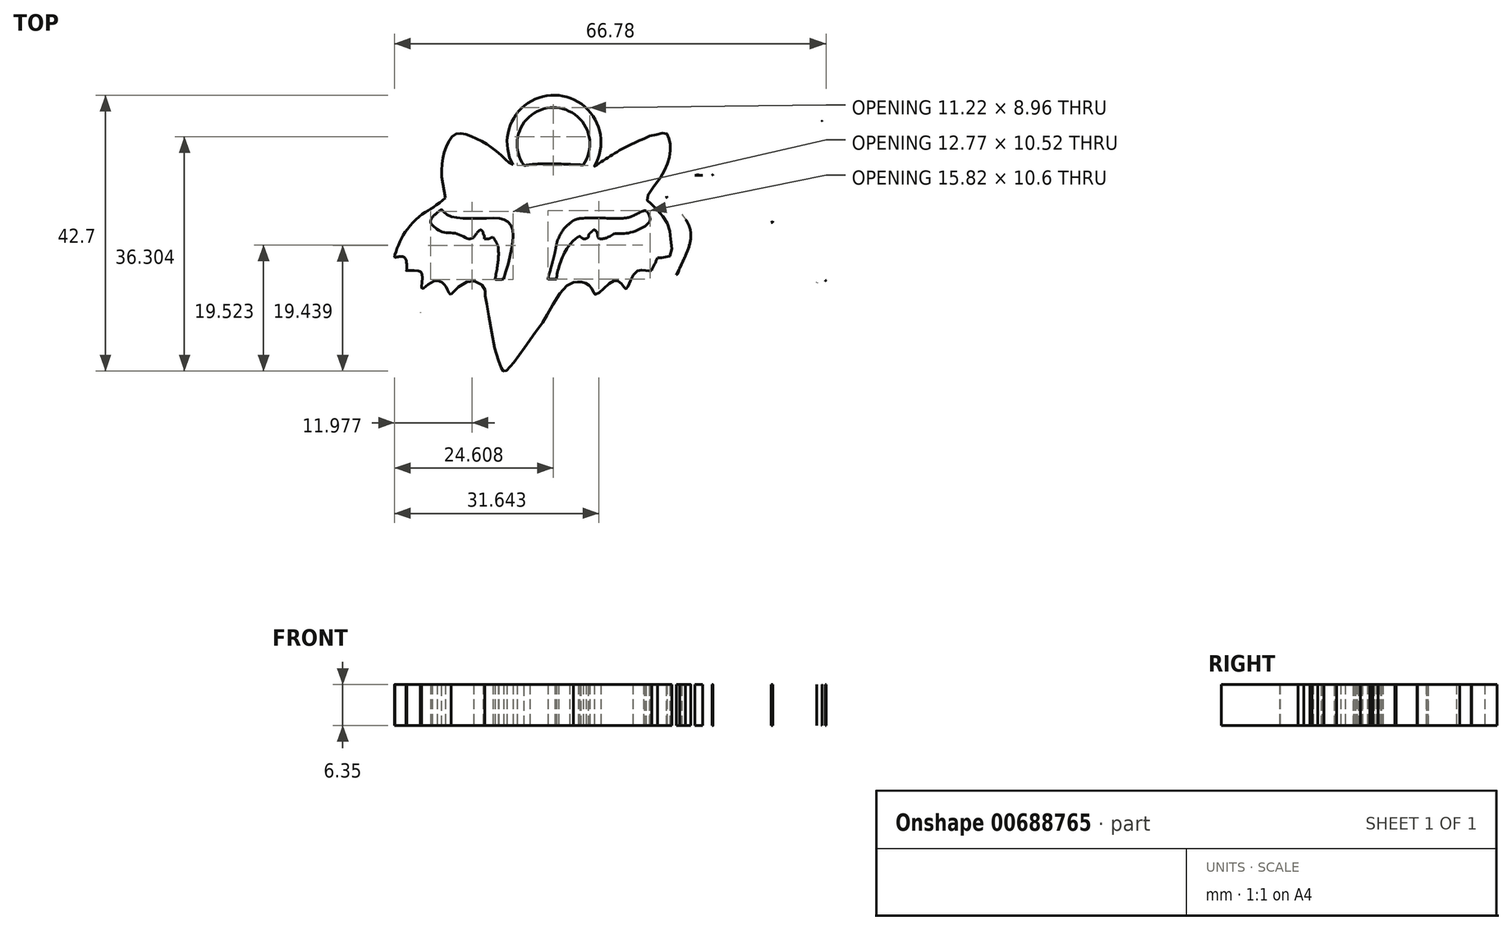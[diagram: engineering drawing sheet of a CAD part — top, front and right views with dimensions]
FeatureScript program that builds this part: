
annotation { "Feature Type Name" : "Feature", "Feature Type Description" : "" }
export const myFeature = defineFeature(function(context is Context, id is Id, definition is map)
    precondition{}
    {
        {
            var Q0;
            Q0=qCreatedBy(makeId("Top.planeOp"),FACE);
            var sketch = newSketch(context, id + "F0", { "sketchPlane" : qUnion([Q0])});
            skSolve(sketch);
        }
        {
            var Q0;
            Q0=qCreatedBy(makeId("Top.planeOp"),FACE);
            var sketch = newSketch(context, id + "F1", { "sketchPlane" : qUnion([Q0])});
            skLineSegment(sketch, "E0", {"start": v(-49.09, -7.95) * mm, "end": v(-49.09, -7.95) * mm});
            skLineSegment(sketch, "E1", {"start": v(-25.67, 10.6) * mm, "end": v(-25.67, 10.9) * mm});
            skFitSpline(sketch, "E2", {"points": [v(-47.91, 14.68) * mm, v(-18.42, 14.68) * mm], "startDerivative": vector(29.5, 0) * mm, "endDerivative": vector(29.5, 0) * mm});
            skFitSpline(sketch, "E3", {"points": [v(-18.42, 14.77) * mm, v(-19.98, 12.11) * mm, v(-20.27, 10.35) * mm, v(-20.02, 7.92) * mm], "startDerivative": vector(-4.98, -7.4) * mm, "endDerivative": vector(1.02, -7.61) * mm});
            skFitSpline(sketch, "E4", {"points": [v(-4, -7.29) * mm, v(-5.22, -7.31) * mm, v(-5.3, -7.27) * mm], "startDerivative": vector(-2, -0.12) * mm, "endDerivative": vector(-0.28, 0.23) * mm});
            skFitSpline(sketch, "E5", {"points": [v(-5.3, -7.27) * mm, v(-4.8, -4.13) * mm, v(-4.8, -2.31) * mm], "startDerivative": vector(1.15, 5.88) * mm, "endDerivative": vector(-0.2, 3.94) * mm});
            skFitSpline(sketch, "E6", {"points": [v(-4.8, -2.31) * mm, v(-5.1, -1.62) * mm, v(-5.66, -0.73) * mm], "startDerivative": vector(-0.57, 1.49) * mm, "endDerivative": vector(-1.14, 1.67) * mm});
            skFitSpline(sketch, "E7", {"points": [v(-5.66, -0.73) * mm, v(-6.33, -1.03) * mm, v(-6.94, -1.03) * mm], "startDerivative": vector(-1.29, -0.72) * mm, "endDerivative": vector(-1.27, 0.14) * mm});
            skFitSpline(sketch, "E8", {"points": [v(-6.94, -1.1) * mm, v(-6.94, -1.03) * mm], "startDerivative": vector(0, 0.07) * mm, "endDerivative": vector(0, 0.07) * mm});
            skFitSpline(sketch, "E9", {"points": [v(-6.94, -1.1) * mm, v(-6.94, -0.48) * mm], "startDerivative": vector(0, 0.63) * mm, "endDerivative": vector(0, 0.63) * mm});
            skFitSpline(sketch, "E10", {"points": [v(-6.94, -0.48) * mm, v(-7.16, -0.32) * mm, v(-7.13, 0) * mm], "startDerivative": vector(-0.6, 0.26) * mm, "endDerivative": vector(0.21, 0.7) * mm});
            skFitSpline(sketch, "E11", {"points": [v(-7.13, 0) * mm, v(-7.56, 0.34) * mm, v(-8.61, -0.86) * mm], "startDerivative": vector(-1.1, 1.43) * mm, "endDerivative": vector(-1.82, -2.79) * mm});
            skFitSpline(sketch, "E12", {"points": [v(-8.61, -0.86) * mm, v(-9.38, -1.03) * mm, v(-11.22, -0.25) * mm, v(-13.42, 0) * mm, v(-15.04, 1.1) * mm], "startDerivative": vector(-4.09, -2) * mm, "endDerivative": vector(-5.54, 5.18) * mm});
            skFitSpline(sketch, "E13", {"points": [v(-15.04, 1.1) * mm, v(-15.29, 1.57) * mm, v(-15.04, 2.26) * mm, v(-14.25, 3) * mm], "startDerivative": vector(-1.25, 1.57) * mm, "endDerivative": vector(2.2, 1.8) * mm});
            skFitSpline(sketch, "E14", {"points": [v(-14.25, 3) * mm, v(-13.92, 3.28) * mm, v(-13.62, 3.51) * mm, v(-13.15, 3) * mm, v(-12.16, 2.43) * mm, v(-10.27, 2.14) * mm, v(-6.94, 2.14) * mm, v(-4.43, 2.12) * mm, v(-3.47, 1.7) * mm, v(-2.7, 0.75) * mm, v(-2.52, -0.98) * mm, v(-3.06, -4.07) * mm, v(-4, -7.29) * mm], "startDerivative": vector(7.65, 5.48) * mm, "endDerivative": vector(-8.33, -25.98) * mm});
            skFitSpline(sketch, "E15", {"points": [v(7.89, -0.68) * mm, v(8.34, -1.01) * mm, v(8.8, -0.99) * mm, v(9.19, -0.68) * mm, v(9.19, -0.43) * mm, v(9.58, 0) * mm, v(10, 0.34) * mm, v(10.47, 0) * mm, v(10.59, -0.68) * mm, v(10.86, -1.01) * mm, v(11.58, -0.99) * mm, v(12.38, -0.68) * mm, v(13.22, -0.26) * mm, v(14.48, -0.21) * mm, v(16.58, 0.24) * mm, v(18.6, 1.67) * mm, v(18.54, 2.58) * mm, v(18.15, 3.22) * mm, v(17.69, 3.29) * mm, v(16.04, 2.52) * mm, v(14.14, 2.13) * mm, v(7.8, 2.12) * mm, v(7.8, 2.1) * mm], "startDerivative": vector(12.59, -11.48) * mm, "endDerivative": vector(1.85, -2.93) * mm});
            skFitSpline(sketch, "E16", {"points": [v(7.83, 2.1) * mm, v(7.8, 2.12) * mm, v(6.21, 1.32) * mm, v(4.53, -0.9) * mm, v(3.98, -3.04) * mm, v(3.6, -4.55) * mm, v(2.86, -7.29) * mm], "startDerivative": vector(-0.8, 0.97) * mm, "endDerivative": vector(-3.68, -13.47) * mm});
            skPoint(sketch, "E17.3.internal.snap0", {"position": v(-53.93, -7) * mm});
            skFitSpline(sketch, "E18", {"points": [v(-21.7, -6.22) * mm, v(-21.7, -8.4) * mm, v(-21.32, -9.37) * mm, v(-20.7, -10) * mm, v(-20.03, -9.32) * mm, v(-19.25, -8.66) * mm, v(-19.1, -9.52) * mm, v(-18.72, -10.73) * mm, v(-18.23, -11.67) * mm, v(-16.87, -12.4) * mm, v(-16.87, -12.46) * mm], "startDerivative": vector(-0.94, -16.44) * mm, "endDerivative": vector(-1.12, -2.05) * mm});
            skFitSpline(sketch, "E19", {"points": [v(-16.87, -12.46) * mm, v(-16.38, -11.54) * mm, v(-15.6, -10.64) * mm, v(-15.05, -10.16) * mm, v(-14.65, -11.22) * mm, v(-14.1, -12.1) * mm, v(-13.36, -12.83) * mm, v(-12.23, -13.45) * mm, v(-12.23, -13.47) * mm], "startDerivative": vector(3.11, 6.8) * mm, "endDerivative": vector(-0.47, -0.82) * mm});
            skFitSpline(sketch, "E20", {"points": [v(-12.23, -13.46) * mm, v(-11.6, -12.44) * mm], "startDerivative": vector(0.62, 1.02) * mm, "endDerivative": vector(0.62, 1.02) * mm});
            skFitSpline(sketch, "E21", {"points": [v(15.9, -10.84) * mm, v(16.57, -10.17) * mm, v(17.08, -9.37) * mm, v(17.42, -8.8) * mm, v(17.78, -8.73) * mm, v(18.08, -9.22) * mm, v(18.2, -9.76) * mm, v(18.44, -9.97) * mm, v(18.82, -9.76) * mm, v(19.28, -9.42) * mm, v(19.85, -8.78) * mm, v(20.32, -8.1) * mm, v(20.66, -7.35) * mm, v(20.67, -7.35) * mm], "startDerivative": vector(6.88, 6.38) * mm, "endDerivative": vector(0.9, -0.5) * mm});
            skFitSpline(sketch, "E22", {"points": [v(14.66, 15.21) * mm, v(17.54, 16.2) * mm, v(21.2, 17) * mm, v(22.88, 17.22) * mm, v(24.07, 14.55) * mm, v(24.17, 11.37) * mm, v(24.18, 11.37) * mm], "startDerivative": vector(13.27, 5.32) * mm, "endDerivative": vector(1.02, 0.5) * mm});
            skFitSpline(sketch, "E23", {"points": [v(24.18, 11.38) * mm, v(21.23, 5.36) * mm, v(21.23, 5.53) * mm], "startDerivative": vector(-4.9, -10.54) * mm, "endDerivative": vector(0.24, 1.82) * mm});
            skFitSpline(sketch, "E24", {"points": [v(21.23, 5.53) * mm, v(23.53, 2.89) * mm, v(24.97, 0) * mm, v(24.18, -3.63) * mm, v(22.73, -6.6) * mm], "startDerivative": vector(9.4, -10.26) * mm, "endDerivative": vector(-6.1, -11.5) * mm});
            skFitSpline(sketch, "E25", {"points": [v(34.28, 1.1) * mm, v(33.07, 2.83) * mm, v(28.3, 8.87) * mm, v(28.42, 8.8) * mm], "startDerivative": vector(-2.16, 3.59) * mm, "endDerivative": vector(2.19, -1.55) * mm});
            skFitSpline(sketch, "E26", {"points": [v(28.42, 8.8) * mm, v(24.18, 8.8) * mm], "startDerivative": vector(-4.24, 0) * mm, "endDerivative": vector(-4.24, 0) * mm});
            skFitSpline(sketch, "E27", {"points": [v(45.28, 17.22) * mm, v(45.28, 17.2) * mm, v(24.18, 17.2) * mm], "startDerivative": vector(0.33, -0.69) * mm, "endDerivative": vector(-32.31, 0.33) * mm});
            skFitSpline(sketch, "E28", {"points": [v(45.29, 17.22) * mm, v(43.56, 9.5) * mm], "startDerivative": vector(-1.72, -7.72) * mm, "endDerivative": vector(-1.72, -7.72) * mm});
            skFitSpline(sketch, "E29", {"points": [v(43.56, 9.5) * mm, v(44.34, 8.34) * mm], "startDerivative": vector(0.78, -1.16) * mm, "endDerivative": vector(0.78, -1.16) * mm});
            skFitSpline(sketch, "E30", {"points": [v(44.34, 8.34) * mm, v(45.69, 9.5) * mm], "startDerivative": vector(1.34, 1.16) * mm, "endDerivative": vector(1.34, 1.16) * mm});
            skFitSpline(sketch, "E31", {"points": [v(47.66, 17.2) * mm, v(68.11, 17.2) * mm], "startDerivative": vector(20.45, 0) * mm, "endDerivative": vector(20.45, 0) * mm});
            skFitSpline(sketch, "E32", {"points": [v(68.11, 17.33) * mm, v(66.26, 8.93) * mm], "startDerivative": vector(-1.85, -8.4) * mm, "endDerivative": vector(-1.85, -8.4) * mm});
            skFitSpline(sketch, "E33", {"points": [v(60.99, 8.93) * mm, v(51.26, 1.06) * mm, v(51.24, 1.02) * mm], "startDerivative": vector(-14.98, -11.94) * mm, "endDerivative": vector(-0.07, -0.46) * mm});
            skFitSpline(sketch, "E34", {"points": [v(16.52, -14.6) * mm, v(16.95, -14.62) * mm], "startDerivative": vector(0.43, -0.01) * mm, "endDerivative": vector(0.43, -0.01) * mm});
            skFitSpline(sketch, "E35", {"points": [v(27.54, 7.05) * mm, v(31.94, 1.5) * mm, v(31.91, 1.48) * mm], "startDerivative": vector(7.07, -8.52) * mm, "endDerivative": vector(-0.53, -0.19) * mm});
            skFitSpline(sketch, "E36", {"points": [v(26.23, -2.36) * mm, v(26.4, -0.97) * mm, v(26.23, 0.64) * mm, v(25.75, 2.5) * mm, v(23.15, 5.64) * mm, v(23.12, 5.59) * mm], "startDerivative": vector(1.34, 6.98) * mm, "endDerivative": vector(-0.1, -1.92) * mm});
            skFitSpline(sketch, "E37", {"points": [v(46.35, -6.63) * mm, v(45.9, -7.47) * mm, v(45.28, -7.81) * mm, v(44.5, -7.81) * mm, v(44.5, -7.78) * mm], "startDerivative": vector(-1.16, -2.79) * mm, "endDerivative": vector(0.23, 0.5) * mm});
            skFitSpline(sketch, "E38", {"points": [v(44.5, -7.78) * mm, v(43.44, -12.63) * mm], "startDerivative": vector(-1.06, -4.85) * mm, "endDerivative": vector(-1.06, -4.85) * mm});
            skFitSpline(sketch, "E39", {"points": [v(-12.98, 5.32) * mm, v(-13.54, 8.65) * mm, v(-13.4, 11.41) * mm, v(-12.71, 13.57) * mm, v(-11.39, 15.2) * mm, v(-9.69, 15.08) * mm, v(-7.6, 14.17) * mm, v(-5.72, 13) * mm, v(-3.75, 11.34) * mm, v(-2.54, 10.43) * mm, v(-0.8, 10.32) * mm, v(2, 10.58) * mm, v(10.05, 10.2) * mm, v(10.08, 10.16) * mm], "startDerivative": vector(-7.87, 36.08) * mm, "endDerivative": vector(0.56, -3.15) * mm});
            skFitSpline(sketch, "E40", {"points": [v(10.08, 10.16) * mm, v(14.05, 12.7) * mm, v(18.65, 14.87) * mm], "startDerivative": vector(7.87, 5.39) * mm, "endDerivative": vector(9.26, 4.03) * mm});
            skFitSpline(sketch, "E41", {"points": [v(18.65, 14.87) * mm, v(20.13, 15.21) * mm, v(21.16, 15.32) * mm, v(21.6, 14.5) * mm, v(21.82, 13.37) * mm, v(21.72, 11.89) * mm, v(21.23, 10.16) * mm, v(20.07, 8.1) * mm, v(18.15, 5.25) * mm, v(18.54, 4.64) * mm, v(20.15, 3.09) * mm, v(21.54, 0.94) * mm, v(21.94, -1.56) * mm, v(21.59, -3.84) * mm, v(19.82, -3.93) * mm, v(19.83, -3.96) * mm], "startDerivative": vector(22.87, 4.8) * mm, "endDerivative": vector(3.6, -3.57) * mm});
            skFitSpline(sketch, "E42", {"points": [v(19.83, -3.96) * mm, v(18.92, -5.95) * mm, v(18.9, -6) * mm], "startDerivative": vector(-1.44, -3.14) * mm, "endDerivative": vector(-0.11, -0.21) * mm});
            skFitSpline(sketch, "E43", {"points": [v(18.92, -5.95) * mm, v(18.15, -5.95) * mm, v(16.45, -6.2) * mm, v(14.98, -8.75) * mm, v(14.38, -8.1) * mm, v(13.02, -7.55) * mm, v(10.31, -9.64) * mm, v(9.69, -8.8) * mm, v(8.4, -7.77) * mm, v(6.84, -7.75) * mm], "startDerivative": vector(-8.8, -0.7) * mm, "endDerivative": vector(-14.52, -1.73) * mm});
            skFitSpline(sketch, "E44", {"points": [v(6.84, -7.75) * mm, v(5.17, -8.86) * mm, v(2.87, -12.64) * mm, v(1.24, -15.11) * mm, v(-3.39, -21.31) * mm, v(-3.82, -21.5) * mm, v(-4.08, -21.47) * mm, v(-4.32, -21.03) * mm, v(-5.22, -18.5) * mm, v(-6.47, -11.76) * mm, v(-6.87, -9.64) * mm, v(-6.87, -8.82) * mm, v(-7.98, -7.75) * mm, v(-9.88, -7.77) * mm, v(-12.09, -9.64) * mm], "startDerivative": vector(-24.53, -10.71) * mm, "endDerivative": vector(-26.27, -28.08) * mm});
            skFitSpline(sketch, "E45", {"points": [v(-12.09, -9.64) * mm, v(-12.43, -9.44) * mm, v(-12.92, -8.4) * mm, v(-13.98, -7.55) * mm, v(-15.15, -7.77) * mm, v(-16.3, -8.6) * mm, v(-16.61, -8.68) * mm, v(-16.6, -6.6) * mm, v(-17.29, -5.95) * mm, v(-19.07, -5.95) * mm, v(-18.98, -5.95) * mm], "startDerivative": vector(-5.61, 1.85) * mm, "endDerivative": vector(4.73, 0.11) * mm});
            skFitSpline(sketch, "E46", {"points": [v(-12.98, 5.32) * mm, v(-14.82, 3.87) * mm, v(-16.38, 2.9) * mm, v(-18.37, 1.07) * mm, v(-19.77, -0.92) * mm, v(-20.59, -2.87) * mm, v(-20.86, -3.89) * mm, v(-20.82, -3.92) * mm], "startDerivative": vector(-10.8, -9.13) * mm, "endDerivative": vector(1.8, -0.8) * mm});
            skFitSpline(sketch, "E47", {"points": [v(-20.82, -3.92) * mm, v(-19.31, -3.92) * mm, v(-18.98, -5.95) * mm], "startDerivative": vector(3.88, 0.87) * mm, "endDerivative": vector(-0.09, -4.78) * mm});
            skFitSpline(sketch, "E48", {"points": [v(-14.8, 18.65) * mm, v(-51.24, 18.6) * mm], "startDerivative": vector(-36.44, -0.05) * mm, "endDerivative": vector(-36.44, -0.05) * mm});
            skFitSpline(sketch, "E49", {"points": [v(45.9, 19.18) * mm, v(46.51, 18.7) * mm, v(47.11, 19.18) * mm, v(47.05, 19.18) * mm], "startDerivative": vector(1.17, -1.83) * mm, "endDerivative": vector(-0.72, -0.2) * mm});
            skFitSpline(sketch, "E50", {"points": [v(47.05, 19.12) * mm, v(68.94, 19.18) * mm, v(69, 19.18) * mm], "startDerivative": vector(33.36, 0.1) * mm, "endDerivative": vector(0.6, 0) * mm});
            skFitSpline(sketch, "E51", {"points": [v(70.13, 17.33) * mm, v(67.86, 8.3) * mm, v(67.5, 7.53) * mm, v(66.88, 7.08) * mm, v(61.43, 7.12) * mm, v(62.89, 6.68) * mm, v(64.3, 6.03) * mm, v(65.52, 5.1) * mm, v(66.49, 3.8) * mm, v(66.88, 2.35) * mm, v(67.08, 0.44) * mm, v(66.48, -1.36) * mm, v(65.5, -2.71) * mm, v(64.05, -3.84) * mm, v(62.77, -4.5) * mm, v(61.87, -4.8) * mm, v(62.77, -4.87) * mm, v(63.78, -5.4) * mm, v(64.4, -6.4) * mm, v(64.28, -7.62) * mm, v(63.85, -9.43) * mm, v(62.41, -15.26) * mm, v(62.1, -15.78) * mm, v(61.84, -16.1) * mm, v(61.55, -16.3) * mm, v(61.23, -16.49) * mm, v(61.34, -16.5) * mm], "startDerivative": vector(-27.67, -120.8) * mm, "endDerivative": vector(15.83, 0.17) * mm});
            skFitSpline(sketch, "E52", {"points": [v(38.2, -16.5) * mm, v(16.28, -16.5) * mm, v(16.27, -16.5) * mm], "startDerivative": vector(-33.14, 0) * mm, "endDerivative": vector(-0.27, 0) * mm});
            skFitSpline(sketch, "E53", {"points": [v(-49.09, -7.95) * mm, v(-49.46, -8.44) * mm], "startDerivative": vector(-0.37, -0.5) * mm, "endDerivative": vector(-0.37, -0.5) * mm});
            skFitSpline(sketch, "E54", {"points": [v(-39.43, -9) * mm, v(-38.96, -9.14) * mm], "startDerivative": vector(0.47, -0.13) * mm, "endDerivative": vector(0.47, -0.13) * mm});
            skPoint(sketch, "E55.start.orphan", {"position": v(5.02, -4.59) * mm});
            skPoint(sketch, "E56.0.internal.orphan", {"position": v(7.6, -0.68) * mm});
            skPoint(sketch, "E56.endDerivative.orphan", {"position": v(7.8, -0.68) * mm});
            skFitSpline(sketch, "E57", {"points": [v(2.86, -7.29) * mm, v(4.2, -7.29) * mm], "startDerivative": vector(1.34, 0) * mm, "endDerivative": vector(1.34, 0) * mm});
            skFitSpline(sketch, "E58", {"points": [v(4.2, -7.29) * mm, v(4.28, -6.64) * mm, v(4.47, -5.79) * mm, v(4.82, -4.69) * mm, v(5.34, -3.4) * mm, v(6.13, -2.1) * mm, v(7.6, -0.68) * mm, v(7.8, -0.68) * mm, v(7.89, -0.68) * mm, v(8.04, -0.82) * mm, v(8.34, -1.01) * mm, v(8.8, -0.99) * mm, v(9.19, -0.68) * mm, v(9.19, -0.43) * mm, v(9.58, 0) * mm, v(10, 0.34) * mm, v(10.47, 0) * mm, v(10.59, -0.68) * mm, v(10.86, -1.01) * mm, v(11.58, -0.99) * mm, v(12.38, -0.68) * mm, v(13.22, -0.26) * mm, v(14.48, -0.21) * mm, v(16.58, 0.24) * mm, v(18.6, 1.67) * mm, v(18.54, 2.58) * mm, v(18.15, 3.22) * mm, v(17.69, 3.29) * mm, v(16.04, 2.52) * mm, v(14.14, 2.13) * mm, v(7.83, 2.1) * mm, v(6.21, 1.32) * mm, v(4.53, -0.9) * mm, v(3.98, -3.04) * mm, v(3.6, -4.55) * mm, v(3.13, -6.3) * mm, v(2.86, -7.29) * mm], "startDerivative": vector(2.77, 28.84) * mm, "endDerivative": vector(-9.04, -33) * mm});
            skPoint(sketch, "E59.1.internal.orphan", {"position": v(27.9, 15.3) * mm});
            skPoint(sketch, "E60.1.internal.orphan", {"position": v(29.24, 10.91) * mm});
            skPoint(sketch, "E61.1.internal.orphan", {"position": v(27.9, 11.11) * mm});
            skPoint(sketch, "E62.1.internal.orphan", {"position": v(41.93, 15.3) * mm});
            skPoint(sketch, "E62.2.internal.orphan", {"position": v(41.94, 15.35) * mm});
            skPoint(sketch, "E63.10.internal.orphan", {"position": v(41.25, 7.05) * mm});
            skPoint(sketch, "E63.11.internal.orphan", {"position": v(40.22, 8.27) * mm});
            skPoint(sketch, "E63.12.internal.orphan", {"position": v(39.44, 9.11) * mm});
            skPoint(sketch, "E63.13.internal.orphan", {"position": v(39.17, 9.5) * mm});
            skPoint(sketch, "E63.15.internal.orphan", {"position": v(40.84, 11.16) * mm});
            skPoint(sketch, "E63.16.internal.orphan", {"position": v(41.1, 11.16) * mm});
            skPoint(sketch, "E63.4.internal.orphan", {"position": v(49.54, 9.5) * mm});
            skPoint(sketch, "E63.5.internal.orphan", {"position": v(46.73, 7.05) * mm});
            skPoint(sketch, "E63.7.internal.orphan", {"position": v(44.14, 5.64) * mm});
            skPoint(sketch, "E63.8.internal.orphan", {"position": v(43.44, 5.64) * mm});
            skPoint(sketch, "E63.startDerivative.orphan", {"position": v(49.28, 11.11) * mm});
            skPoint(sketch, "E64.1.internal.orphan", {"position": v(35.4, -12.63) * mm});
            skPoint(sketch, "E65.1.internal.orphan", {"position": v(20.32, -11.56) * mm});
            skPoint(sketch, "E65.start.orphan", {"position": v(20.18, -12.63) * mm});
            skPoint(sketch, "E66.5.internal.orphan", {"position": v(35.4, -7.24) * mm});
            skPoint(sketch, "E66.6.internal.orphan", {"position": v(35.4, -6.88) * mm});
            skPoint(sketch, "E67.1.internal.orphan", {"position": v(39.17, -3.72) * mm});
            skPoint(sketch, "E67.2.internal.orphan", {"position": v(40.8, -3.04) * mm});
            skPoint(sketch, "E67.3.internal.orphan", {"position": v(43.38, -3.04) * mm});
            skPoint(sketch, "E67.5.internal.orphan", {"position": v(46.03, -5.7) * mm});
            skPoint(sketch, "E68.1.internal.orphan", {"position": v(58.77, -12.63) * mm});
            skPoint(sketch, "E68.2.internal.orphan", {"position": v(58.86, -12.63) * mm});
            skPoint(sketch, "E69.1.internal.orphan", {"position": v(52.7, -3.92) * mm});
            skPoint(sketch, "E70.0.internal.orphan", {"position": v(59.63, -8.44) * mm});
            skPoint(sketch, "E70.1.internal.orphan", {"position": v(57.17, -8.44) * mm});
            skPoint(sketch, "E70.2.internal.orphan", {"position": v(57.13, -8.44) * mm});
            skPoint(sketch, "E71.1.internal.orphan", {"position": v(50, 15.3) * mm});
            skPoint(sketch, "E72.end.orphan", {"position": v(49.1, 11.16) * mm});
            skPoint(sketch, "E72.start.orphan", {"position": v(50, 15.35) * mm});
            skPoint(sketch, "E73.1.internal.orphan", {"position": v(63.84, 10.91) * mm});
            skPoint(sketch, "E73.2.internal.orphan", {"position": v(63.88, 10.91) * mm});
            skPoint(sketch, "E74.end.orphan", {"position": v(64.87, 15.3) * mm});
            skPoint(sketch, "E75.startDerivative.orphan", {"position": v(46.35, 12.07) * mm});
            skPoint(sketch, "E76.startDerivative.orphan", {"position": v(47.15, -14.56) * mm});
            skPoint(sketch, "E77.0.internal.orphan", {"position": v(40.22, -14.53) * mm});
            skPoint(sketch, "E77.1.internal.orphan", {"position": v(42.06, -6.4) * mm});
            skPoint(sketch, "E77.startDerivative.orphan", {"position": v(40.84, -11.82) * mm});
            skPoint(sketch, "E78.1.internal.orphan", {"position": v(37.92, -14.56) * mm});
            skPoint(sketch, "E78.startDerivative.orphan", {"position": v(39.17, -9.12) * mm});
            skPoint(sketch, "E79.1.internal.orphan", {"position": v(39.8, -6.4) * mm});
            skPoint(sketch, "E79.startDerivative.orphan", {"position": v(40.8, -5.7) * mm});
            skPoint(sketch, "E80.1.internal.orphan", {"position": v(48.07, 1.06) * mm});
            skPoint(sketch, "E81.end.orphan", {"position": v(60.15, 10.91) * mm});
            skPoint(sketch, "E82.1.internal.orphan", {"position": v(24.18, 9.95) * mm});
            skPoint(sketch, "E82.2.internal.orphan", {"position": v(25.08, 11.37) * mm});
            skPoint(sketch, "E83.endDerivative.orphan", {"position": v(31.22, -0.97) * mm});
            skPoint(sketch, "E83.startDerivative.orphan", {"position": v(28.15, -3.04) * mm});
            skPoint(sketch, "E84.end.orphan", {"position": v(25.08, -5.1) * mm});
            skPoint(sketch, "E85.endDerivative.orphan", {"position": v(56.06, -3.92) * mm});
            skPoint(sketch, "E86.0.internal.orphan", {"position": v(58.46, -6.4) * mm});
            skPoint(sketch, "E86.1.internal.orphan", {"position": v(62.77, -6.4) * mm});
            skPoint(sketch, "E87.1.internal.orphan", {"position": v(60.99, -14.76) * mm});
            skPoint(sketch, "E87.2.internal.orphan", {"position": v(60.99, -14.62) * mm});
            skFitSpline(sketch, "E88", {"points": [v(24.18, 17.2) * mm, v(25.08, 11.37) * mm, v(24.18, 9.95) * mm, v(24.18, 8.8) * mm, v(25.6, 8.8) * mm, v(27, 8.8) * mm, v(28.36, 8.85) * mm, v(28.42, 8.8) * mm], "startDerivative": vector(6.68, -24.74) * mm, "endDerivative": vector(1, -1.51) * mm});
            skFitSpline(sketch, "E89", {"points": [v(37.68, 1.65) * mm, v(20.32, -11.56) * mm, v(20.18, -12.63) * mm], "startDerivative": vector(-29.6, -20.36) * mm, "endDerivative": vector(1.1, -4.94) * mm});
            skFitSpline(sketch, "E90", {"points": [v(36.42, -7.87) * mm, v(35.4, -7.24) * mm, v(35.4, -6.88) * mm, v(39.17, -3.72) * mm, v(40.8, -3.04) * mm, v(43.38, -3.04) * mm, v(46.03, -5.7) * mm, v(46.35, -6.63) * mm, v(45.9, -7.47) * mm, v(45.28, -7.81) * mm, v(44.5, -7.78) * mm, v(44.15, -9.4) * mm, v(43.8, -11.01) * mm, v(43.44, -12.63) * mm], "startDerivative": vector(-18.94, 9.98) * mm, "endDerivative": vector(-4.26, -21.04) * mm});
            skFitSpline(sketch, "E91", {"points": [v(58.86, -12.63) * mm, v(43.44, -12.63) * mm], "startDerivative": vector(-15.42, 0) * mm, "endDerivative": vector(-15.42, 0) * mm});
            skFitSpline(sketch, "E92", {"points": [v(41.94, 15.35) * mm, v(41.1, 11.16) * mm], "startDerivative": vector(-0.85, -4.19) * mm, "endDerivative": vector(-0.85, -4.19) * mm});
            skFitSpline(sketch, "E93", {"points": [v(41.1, 11.16) * mm, v(40.84, 11.16) * mm, v(39.17, 9.5) * mm, v(39.44, 9.11) * mm, v(40.22, 8.27) * mm, v(41.25, 7.05) * mm, v(43.44, 5.64) * mm, v(44.14, 5.64) * mm, v(46.73, 7.05) * mm, v(49.54, 9.5) * mm, v(49.28, 11.11) * mm], "startDerivative": vector(-4.41, 2.3) * mm, "endDerivative": vector(-6.82, 15.52) * mm});
            skFitSpline(sketch, "E94", {"points": [v(49.28, 11.11) * mm, v(49.1, 11.16) * mm, v(50, 15.35) * mm], "startDerivative": vector(-1.24, -0.16) * mm, "endDerivative": vector(2, 7.06) * mm});
            skFitSpline(sketch, "E95", {"points": [v(40.84, 11.16) * mm, v(40.04, 10.87) * mm, v(39.53, 10.48) * mm, v(39.2, 10.1) * mm, v(39.17, 9.5) * mm], "startDerivative": vector(-2.98, -0.82) * mm, "endDerivative": vector(0.2, -2.7) * mm});
            skFitSpline(sketch, "E96", {"points": [v(63.88, 10.91) * mm, v(63.84, 10.91) * mm, v(60.15, 10.91) * mm], "startDerivative": vector(-0.24, 0) * mm, "endDerivative": vector(-5.73, 0) * mm});
            skPoint(sketch, "E97.1.internal.orphan", {"position": v(-35.18, -5.1) * mm});
            skPoint(sketch, "E97.2.internal.orphan", {"position": v(-34.84, -5.1) * mm});
            skPoint(sketch, "E97.3.internal.orphan", {"position": v(-33.24, -5.1) * mm});
            skPoint(sketch, "E97.4.internal.orphan", {"position": v(-31.14, -5.1) * mm});
            skPoint(sketch, "E97.5.internal.orphan", {"position": v(-26.01, -5.1) * mm});
            skPoint(sketch, "E98.right.end.orphan", {"position": v(-32.85, 6.76) * mm});
            skPoint(sketch, "E99.1.internal.orphan", {"position": v(-24.99, 9.6) * mm});
            skPoint(sketch, "E100.1.internal.orphan", {"position": v(-36.35, 9.6) * mm});
            skPoint(sketch, "E101.12.internal.orphan", {"position": v(-35.18, -5.29) * mm});
            skPoint(sketch, "E101.3.internal.orphan", {"position": v(-32.85, -15.53) * mm});
            skPoint(sketch, "E102.3.internal.orphan", {"position": v(-40.22, -5.43) * mm});
            skPoint(sketch, "E103.start.orphan", {"position": v(-37.36, -7) * mm});
            skPoint(sketch, "E104.14.internal.orphan", {"position": v(-52.8, -5.43) * mm});
            skPoint(sketch, "E104.17.internal.orphan", {"position": v(-57.63, -6.4) * mm});
            skPoint(sketch, "E105.start.orphan", {"position": v(-52.58, 8.2) * mm});
            skPoint(sketch, "E106.0.internal.orphan", {"position": v(-45.15, 8.2) * mm});
            skPoint(sketch, "E106.1.internal.orphan", {"position": v(-45.15, 9.36) * mm});
            skPoint(sketch, "E106.end.orphan", {"position": v(-48.96, 10.35) * mm});
            skPoint(sketch, "E107.orphan", {"position": v(-51.8, -7) * mm});
            skPoint(sketch, "E108.end.orphan", {"position": v(-56.07, -7) * mm});
            skPoint(sketch, "E109.end.orphan", {"position": v(-36.21, -9.14) * mm});
            skPoint(sketch, "E109.start.orphan", {"position": v(-37.11, -12.83) * mm});
            skPoint(sketch, "E110.21.internal.orphan", {"position": v(54.1, 0) * mm});
            skFitSpline(sketch, "E111.trimOffspring", {"points": [v(27.9, 11.11) * mm, v(29.24, 10.91) * mm, v(37.45, 1.49) * mm, v(37.68, 1.65) * mm], "startDerivative": vector(4.49, 2.04) * mm, "endDerivative": vector(1.27, 3.27) * mm});
            skPoint(sketch, "E112.1.internal.orphan", {"position": v(39.63, -16.5) * mm});
            skPoint(sketch, "E113.1.internal.orphan", {"position": v(38.9, -16.3) * mm});
            skPoint(sketch, "E113.3.internal.orphan", {"position": v(38.24, -16.5) * mm});
            skPoint(sketch, "E114.3.internal.orphan", {"position": v(9.53, 14.21) * mm});
            skPoint(sketch, "E114.4.internal.orphan", {"position": v(9.5, 14.21) * mm});
            skPoint(sketch, "E115.1.internal.orphan", {"position": v(-13.78, 18.65) * mm});
            skPoint(sketch, "E115.4.internal.orphan", {"position": v(-9.6, 18.65) * mm});
            skPoint(sketch, "E115.end.orphan", {"position": v(-0.8, 14.21) * mm});
            skPoint(sketch, "E116.1.internal.orphan", {"position": v(23.53, 6.19) * mm});
            skPoint(sketch, "E117.startDerivative.orphan", {"position": v(29.24, -0.3) * mm});
            skPoint(sketch, "E118.1.internal.orphan", {"position": v(21.25, -6.2) * mm});
            skPoint(sketch, "E119.18.internal.orphan", {"position": v(5.02, -16.5) * mm});
            skPoint(sketch, "E120.4.internal.orphan", {"position": v(-25.29, -5.29) * mm});
            skPoint(sketch, "E121.8.internal.orphan", {"position": v(-9.49, -19.56) * mm});
            skPoint(sketch, "E122.1.internal.orphan", {"position": v(-16.75, 11.37) * mm});
            skFitSpline(sketch, "E123", {"points": [v(21.23, 5.53) * mm, v(22.02, 4.67) * mm, v(23.53, 2.89) * mm, v(24.97, 0) * mm, v(24.18, -3.63) * mm, v(23.22, -5.66) * mm, v(22.73, -6.6) * mm, v(21.25, -6.2) * mm, v(20.67, -7.35) * mm], "startDerivative": vector(7.63, -8.24) * mm, "endDerivative": vector(-3.19, -16.17) * mm});
            skPoint(sketch, "E124.4.internal.orphan", {"position": v(-25.3, -4.59) * mm});
            skPoint(sketch, "E125.4.internal.orphan", {"position": v(-17.69, 5.53) * mm});
            skPoint(sketch, "E125.5.internal.orphan", {"position": v(-17.62, 5.44) * mm});
            skFitSpline(sketch, "E126", {"points": [v(-13.4, 16.85) * mm, v(-12.66, 17.78) * mm, v(-11.43, 18.88) * mm, v(-9.6, 18.65) * mm, v(-6.6, 17.78) * mm, v(-4.25, 16.85) * mm, v(-1.85, 15.08) * mm, v(-0.8, 14.21) * mm, v(0.81, 14.21) * mm, v(9.5, 14.21) * mm, v(10.04, 14.21) * mm, v(11.13, 15.08) * mm, v(14.05, 16.52) * mm, v(17.61, 17.97) * mm, v(21.23, 18.65) * mm, v(23, 19.12) * mm], "startDerivative": vector(14.37, 18.43) * mm, "endDerivative": vector(27.3, 8.38) * mm});
            skFitSpline(sketch, "E127", {"points": [v(25.08, -5.1) * mm, v(23.12, -7.63) * mm, v(21.77, -7.22) * mm, v(21.23, -8.7) * mm, v(19.92, -10.08) * mm, v(18.73, -11.16) * mm, v(18, -10.98) * mm, v(17.56, -10.08) * mm, v(17.04, -10.98) * mm, v(15.99, -12.19) * mm, v(14.5, -13.17) * mm, v(12.99, -13.37) * mm, v(11.85, -13.31) * mm, v(9.88, -14.6) * mm, v(7.74, -15.05) * mm, v(6.58, -14.25) * mm, v(5.65, -15.45) * mm, v(4.09, -17.9) * mm, v(2.32, -20.14) * mm, v(1.06, -21.74) * mm, v(-0.46, -23.21) * mm, v(-2.24, -24.82) * mm, v(-4.38, -25.66) * mm, v(-6, -25.4) * mm, v(-7.1, -24.55) * mm, v(-8.04, -23.17) * mm, v(-9.49, -19.56) * mm, v(-10.1, -17.24) * mm, v(-10.67, -14.16) * mm, v(-11.06, -14.57) * mm, v(-11.73, -15.03) * mm, v(-13, -15.04) * mm, v(-13.98, -14.4) * mm, v(-14.78, -13.8) * mm, v(-15.57, -13.2) * mm, v(-15.83, -13.45) * mm, v(-16.77, -13.87) * mm, v(-18.06, -13.7) * mm, v(-18.88, -13.26) * mm, v(-19.6, -12.66) * mm, v(-20.14, -11.72) * mm, v(-20.67, -11.72) * mm, v(-22.18, -11.22) * mm, v(-23.03, -9.97) * mm, v(-23.45, -8.7) * mm, v(-24.42, -8.2) * mm, v(-25.01, -6.94) * mm, v(-25.29, -5.29) * mm, v(-25.3, -4.59) * mm, v(-25.3, -3.32) * mm, v(-24.42, -1.13) * mm, v(-23.04, 2.14) * mm, v(-21.2, 3.88) * mm, v(-17.62, 5.44) * mm, v(-16.6, 5.44) * mm, v(-17.1, 6.8) * mm, v(-16.75, 11.37) * mm, v(-15.2, 14.5) * mm, v(-13.2, 17.1) * mm, v(-13.17, 17.14) * mm], "startDerivative": vector(-76.29, -158.05) * mm, "endDerivative": vector(4.76, 6.82) * mm});
            skPoint(sketch, "E128.5.internal.orphan", {"position": v(25.08, 14.26) * mm});
            skPoint(sketch, "E129.endDerivative.orphan", {"position": v(2.32, 12.6) * mm});
            skPoint(sketch, "E130.2.internal.orphan", {"position": v(-14.8, 14.02) * mm});
            skPoint(sketch, "E130.5.internal.orphan", {"position": v(-10.27, 17) * mm});
            skPoint(sketch, "E131.2.internal.orphan", {"position": v(-22.25, 0) * mm});
            skPoint(sketch, "E131.end.orphan", {"position": v(-16.15, 9.95) * mm});
            skPoint(sketch, "E17.1.internal.orphan", {"position": v(-23.42, -4.59) * mm});
            skPoint(sketch, "E17.3.internal.orphan", {"position": v(-23.18, -7) * mm});
            skPoint(sketch, "E17.startDerivative.orphan", {"position": v(-23.37, -3.63) * mm});
            skPoint(sketch, "E132.1.internal.orphan", {"position": v(-7.74, -19.56) * mm});
            skPoint(sketch, "E133.0.internal.orphan", {"position": v(8.08, -11.96) * mm});
            skPoint(sketch, "E133.1.internal.orphan", {"position": v(8.22, -12.44) * mm});
            skPoint(sketch, "E133.10.internal.orphan", {"position": v(14.7, -11.96) * mm});
            skPoint(sketch, "E133.5.internal.orphan", {"position": v(10.47, -12.44) * mm});
            skFitSpline(sketch, "E134", {"points": [v(0, 10.32) * mm, v(0.8, 11.48) * mm, v(1.74, 12.27) * mm, v(3.5, 12.6) * mm, v(5.61, 12.06) * mm, v(6.51, 11) * mm, v(6.77, 10.48) * mm], "startDerivative": vector(4.53, 7.26) * mm, "endDerivative": vector(2, -4.41) * mm});
            skPoint(sketch, "E135.1.internal.orphan", {"position": v(0, 12.22) * mm});
            skArc(sketch, "E136", {"start": v(10.05, 10.2) * mm, "mid": v(3.95, 21.2) * mm, "end": v(-2.54, 10.43) * mm});
            skArc(sketch, "E137", {"start": v(8.32, 10.39) * mm, "mid": v(3.7, 19.27) * mm, "end": v(-0.8, 10.32) * mm});
            skSolve(sketch);
        }
        {
            var Q0;
            Q0=makeQuery(id+"F1.imprint","IMPRINT",FACE,{"disambiguationData":[TD([[makeQuery(id+"F1.imprint","IMPRINT",EDGE,{"derivedFrom":sQuery(id+"F1.wireOp",EDGE,"E18")}),-1.0]])]});
            var Q1;
            {var subQ0=sQuery(id+"F1.wireOp",EDGE,"E28");var subQ1=sQuery(id+"F1.wireOp",EDGE,"E27");var subQ2=makeQuery(id+"F1.imprint","INTERSECT",VERTEX,{"disambiguationData":[OD(0.0)],"derivedFrom":[subQ1,subQ0]});Q1=makeQuery(id+"F1.imprint","IMPRINT",FACE,{"disambiguationData":[TD([[makeQuery(id+"F1.imprint","IMPRINT",EDGE,{"disambiguationData":[TD([[subQ2,1.0]])],"derivedFrom":subQ1}),-1.0]])]});}
            var Q2;
            Q2=makeQuery(id+"F1.imprint","IMPRINT",FACE,{"disambiguationData":[TD([[makeQuery(id+"F1.imprint","IMPRINT",EDGE,{"derivedFrom":sQuery(id+"F1.wireOp",EDGE,"E37")}),-1.0]])]});
            var Q3;
            {var subQ0=sQuery(id+"F1.wireOp",EDGE,"E47");var subQ1=sQuery(id+"F1.wireOp",EDGE,"E45");var subQ2=makeQuery(id+"F1.imprint","INTERSECT",VERTEX,{"disambiguationData":[OD(0.0)],"derivedFrom":[subQ1,subQ0]});Q3=makeQuery(id+"F1.imprint","IMPRINT",FACE,{"disambiguationData":[TD([[makeQuery(id+"F1.imprint","IMPRINT",EDGE,{"disambiguationData":[TD([[subQ2,1.0]])],"derivedFrom":subQ1}),1.0]])]});}
            var Q4;
            Q4=makeQuery(id+"F1.imprint","IMPRINT",FACE,{"disambiguationData":[TD([[makeQuery(id+"F1.imprint","IMPRINT",EDGE,{"derivedFrom":sQuery(id+"F1.wireOp",EDGE,"E89")}),1.0]])]});
            var Q5;
            {var subQ0=sQuery(id+"F1.wireOp",EDGE,"E24");Q5=makeQuery(id+"F1.imprint","IMPRINT",FACE,{"disambiguationData":[TD([[makeQuery(id+"F1.imprint","IMPRINT",EDGE,{"derivedFrom":subQ0}),1.0]])]});}
            var Q6;
            {var subQ0=sQuery(id+"F1.wireOp",EDGE,"E24");Q6=makeQuery(id+"F1.imprint","IMPRINT",FACE,{"disambiguationData":[TD([[makeQuery(id+"F1.imprint","IMPRINT",EDGE,{"derivedFrom":subQ0}),-1.0]])]});}
            var Q7;
            {var subQ0=sQuery(id+"F1.wireOp",EDGE,"E88");var subQ1=sQuery(id+"F1.wireOp",EDGE,"E25");var subQ2=makeQuery(id+"F1.imprint","INTERSECT",VERTEX,{"disambiguationData":[OD(0.0)],"derivedFrom":[subQ1,subQ0]});Q7=makeQuery(id+"F1.imprint","IMPRINT",FACE,{"disambiguationData":[TD([[makeQuery(id+"F1.imprint","IMPRINT",EDGE,{"disambiguationData":[TD([[subQ2,-1.0]])],"derivedFrom":subQ1}),-1.0]])]});}
            var Q8;
            {var subQ0=sQuery(id+"F1.wireOp",EDGE,"E88");var subQ1=sQuery(id+"F1.wireOp",EDGE,"E25");var subQ3=makeQuery(id+"F1.imprint","INTERSECT",VERTEX,{"disambiguationData":[OD(1.0)],"derivedFrom":[subQ1,subQ0]});Q8=makeQuery(id+"F1.imprint","IMPRINT",FACE,{"disambiguationData":[TD([[makeQuery(id+"F1.imprint","IMPRINT",EDGE,{"disambiguationData":[TD([[subQ3,-1.0]])],"derivedFrom":subQ1}),1.0]])]});}
            var Q9;
            {var subQ0=sQuery(id+"F1.wireOp",EDGE,"E26");Q9=makeQuery(id+"F1.imprint","IMPRINT",FACE,{"disambiguationData":[TD([[makeQuery(id+"F1.imprint","IMPRINT",EDGE,{"derivedFrom":subQ0}),-1.0]])]});}
            var Q10;
            Q10=makeQuery(id+"F1.imprint","IMPRINT",FACE,{"disambiguationData":[TD([[makeQuery(id+"F1.imprint","IMPRINT",EDGE,{"derivedFrom":sQuery(id+"F1.wireOp",EDGE,"E4")}),1.0]])]});
            var Q11;
            Q11 = qSketchRegion(id + "F0", true);
            var Q12;
            {var subQ0=sQuery(id+"F1.wireOp",EDGE,"E136");Q12=makeQuery(id+"F1.imprint","IMPRINT",FACE,{"disambiguationData":[TD([[makeQuery(id+"F1.imprint","IMPRINT",EDGE,{"derivedFrom":subQ0}),1.0]])]});}
            extrude(context, id + "F2", {"entities" : qUnion([Q0, Q1, Q2, Q3, Q4, Q5, Q6, Q7, Q8, Q9, Q10, Q11, Q12]), "depth" : 6.35 * mm, "offsetDistance" : 25.4 * mm});
        }
    });
